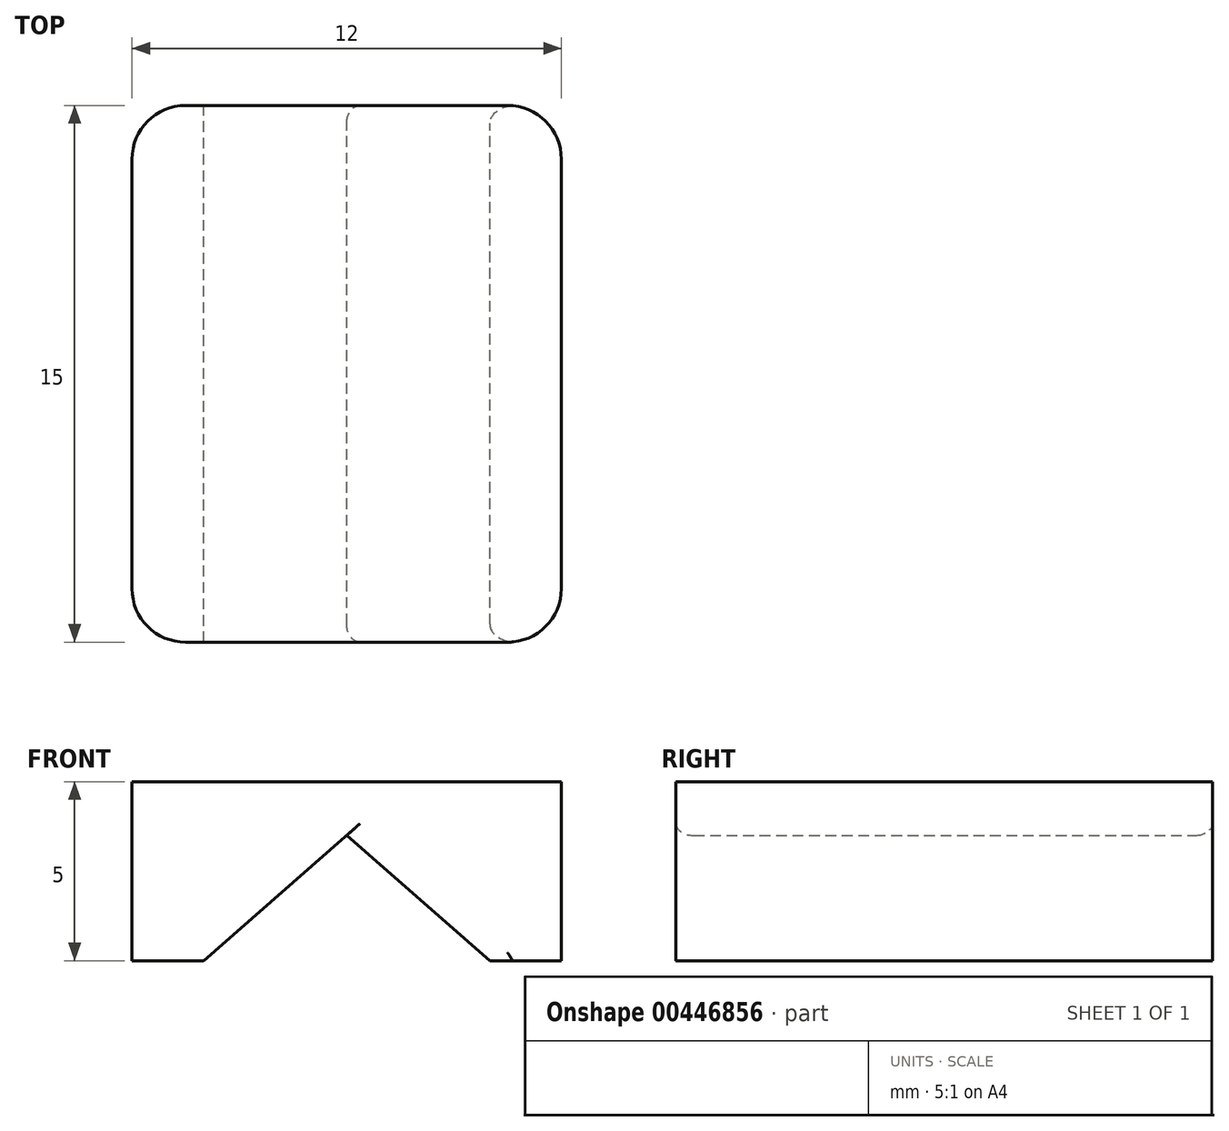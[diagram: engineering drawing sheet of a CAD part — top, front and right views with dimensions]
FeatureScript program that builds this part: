
annotation { "Feature Type Name" : "Feature", "Feature Type Description" : "" }
export const myFeature = defineFeature(function(context is Context, id is Id, definition is map)
    precondition{}
    {
        {
            var Q0;
            Q0=qCreatedBy(makeId("Front.planeOp"),FACE);
            var sketch = newSketch(context, id + "F0", { "sketchPlane" : qUnion([Q0])});
            skLineSegment(sketch, "E0.bottom", {"start": v(0, 0) * mm, "end": v(12, 0) * mm});
            skLineSegment(sketch, "E0.top", {"start": v(0, 5) * mm, "end": v(12, 5) * mm});
            skLineSegment(sketch, "E0.left", {"start": v(0, 0) * mm, "end": v(0, 5) * mm});
            skLineSegment(sketch, "E0.right", {"start": v(12, 0) * mm, "end": v(12, 5) * mm});
            skLineSegment(sketch, "E1", {"start": v(6, 3.5) * mm, "end": v(2, 0) * mm});
            skPoint(sketch, "E1.startSnap0", {"position": v(6, 5) * mm});
            skLineSegment(sketch, "E2", {"start": v(2, 0) * mm, "end": v(6, 3.5) * mm});
            skLineSegment(sketch, "E3", {"start": v(6, 3.5) * mm, "end": v(10, 0) * mm});
            skCircle(sketch, "E4", {"center": v(6, -0.92) * mm, "radius": 3.33 * mm, "construction": true});
            skSolve(sketch);
        }
        {
            var Q0;
            Q0=makeQuery(id+"F0.imprint","IMPRINT",FACE,{"disambiguationData":[TD([[makeQuery(id+"F0.imprint","IMPRINT",EDGE,{"derivedFrom":sQuery(id+"F0.wireOp",EDGE,"E0.top")}),-1.0]])]});
            extrude(context, id + "F1", {"entities" : qUnion([Q0]), "depth" : 15 * mm});
        }
        {
            var Q0;
            Q0=makeQuery(id+"F1.opExtrude","CAP_EDGE",EDGE,{"disambiguationData":[OSD([sQuery(id+"F0.wireOp",EDGE,"E0.left")])],"isStart":false});
            var Q1;
            Q1=makeQuery(id+"F1.opExtrude","CAP_EDGE",EDGE,{"disambiguationData":[OSD([sQuery(id+"F0.wireOp",EDGE,"E0.right")])],"isStart":false});
            var Q2;
            Q2=makeQuery(id+"F1.opExtrude","CAP_EDGE",EDGE,{"disambiguationData":[OSD([sQuery(id+"F0.wireOp",EDGE,"E0.right")])],"isStart":true});
            var Q3;
            Q3=makeQuery(id+"F1.opExtrude","CAP_EDGE",EDGE,{"disambiguationData":[OSD([sQuery(id+"F0.wireOp",EDGE,"E0.left")])],"isStart":true});
            fillet(context, id + "F2", {"entities" : qUnion([Q0, Q1, Q2, Q3]), "radius" : 1.5 * mm, "tangentPropagation" : true, "allowEdgeOverflow" : false});
        }
        {
            var Q0;
            Q0=makeQuery(id+"F1.opExtrude","CAP_EDGE",EDGE,{"disambiguationData":[OSD([sQuery(id+"F0.wireOp",EDGE,"E2")])],"isStart":false});
            var Q1;
            Q1=makeQuery(id+"F1.opExtrude","CAP_EDGE",EDGE,{"disambiguationData":[OSD([sQuery(id+"F0.wireOp",EDGE,"E3")])],"isStart":false});
            var Q2;
            Q2=makeQuery(id+"F1.opExtrude","CAP_EDGE",EDGE,{"disambiguationData":[OSD([sQuery(id+"F0.wireOp",EDGE,"E2")])],"isStart":true});
            var Q3;
            Q3=makeQuery(id+"F1.opExtrude","CAP_EDGE",EDGE,{"disambiguationData":[OSD([sQuery(id+"F0.wireOp",EDGE,"E3")])],"isStart":true});
            fillet(context, id + "F3", {"entities" : qUnion([Q0, Q1, Q2, Q3]), "radius" : 0.5 * mm, "tangentPropagation" : true, "allowEdgeOverflow" : false});
        }
    });
